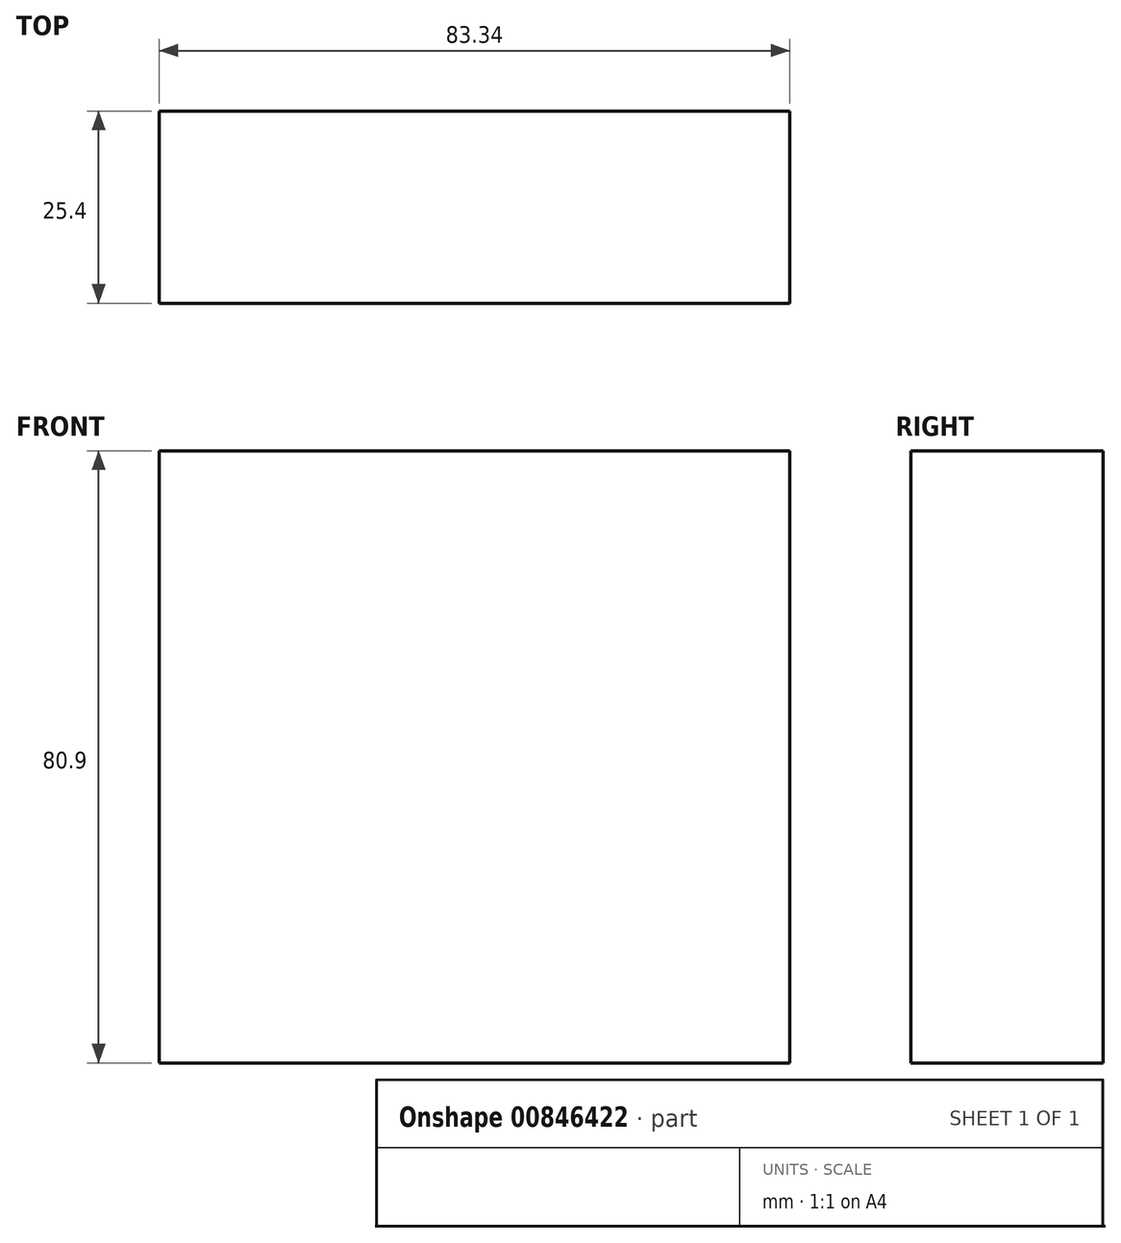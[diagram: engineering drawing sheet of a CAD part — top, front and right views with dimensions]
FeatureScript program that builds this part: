
annotation { "Feature Type Name" : "Feature", "Feature Type Description" : "" }
export const myFeature = defineFeature(function(context is Context, id is Id, definition is map)
    precondition{}
    {
        {
            var Q0;
            Q0=qCreatedBy(makeId("Front.planeOp"),FACE);
            var sketch = newSketch(context, id + "F0", { "sketchPlane" : qUnion([Q0])});
            skLineSegment(sketch, "E0.bottom", {"start": v(-37.88, -31.28) * mm, "end": v(45.46, -31.28) * mm});
            skLineSegment(sketch, "E0.top", {"start": v(-37.88, 49.62) * mm, "end": v(45.46, 49.62) * mm});
            skLineSegment(sketch, "E0.left", {"start": v(-37.88, -31.28) * mm, "end": v(-37.88, 49.62) * mm});
            skLineSegment(sketch, "E0.right", {"start": v(45.46, -31.28) * mm, "end": v(45.46, 49.62) * mm});
            skSolve(sketch);
        }
        {
            var Q0;
            Q0=makeQuery(id+"F0.imprint","IMPRINT",FACE,{"disambiguationData":[TD([[makeQuery(id+"F0.imprint","IMPRINT",EDGE,{"derivedFrom":sQuery(id+"F0.wireOp",EDGE,"E0.bottom")}),1.0]])]});
            var sketch = newSketch(context, id + "F1", { "sketchPlane" : qUnion([Q0])});
            skSolve(sketch);
        }
        {
            var Q0;
            Q0=makeQuery(id+"F1.imprint","IMPRINT",FACE,{"disambiguationData":[TD([[makeQuery(id+"F1.imprint","IMPRINT",EDGE,{"derivedFrom":makeQuery(id+"F0.imprint","IMPRINT",EDGE,{"derivedFrom":sQuery(id+"F0.wireOp",EDGE,"E0.bottom")})}),1.0]])]});
            extrude(context, id + "F2", {"entities" : qUnion([Q0]), "depth" : 25.4 * mm, "offsetDistance" : 25.4 * mm});
        }
    });
